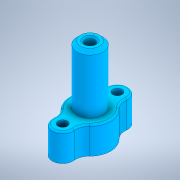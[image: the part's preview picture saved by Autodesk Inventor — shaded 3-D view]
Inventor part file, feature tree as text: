
AUTODESK INVENTOR PART (.ipt)
format: ipt  version: 2020 (Build 240168000, 168)  size: 187,904 bytes
history: native  units: mm
features: fillet x2, sketch x2, revolve x1, chamfer x1, extrude x1
ambient origin geometry x8: Origin, YZ Plane, XZ Plane, XY Plane, X Axis, Y Axis, Z Axis, Center Point
bodies: Solid1 (feature_tree)
feature tree (7):
  revolve  "Revolution1"  [1 undecoded]
  chamfer  "Chamfer1"  Distance=3.8mm
  extrude  "Extrusion3"  Depth=0.5mm TaperAngle=45.0deg
  fillet  "Fillet1"  Radius=6.0mm
  fillet  "Fillet2"  Radius=8.0mm
  sketch  "Sketch1"  dims[d1=1.4mm d8=1.0mm]
  sketch  "Sketch6"  dims[d9=90.0deg d20=3.8mm d21=0.5mm d22=2.0mm d23=45.0deg d24=6.0mm d26=8.0mm d27=12.0mm d28=2.7mm d29=8.0mm d30=0.0mm d31=4.0mm d32=0.5mm]
note: 1 required parameter value undecoded (feature->parameter linkage not recoverable at this tier; creation-order binding heuristic only, values carry confidence <= 0.55)
